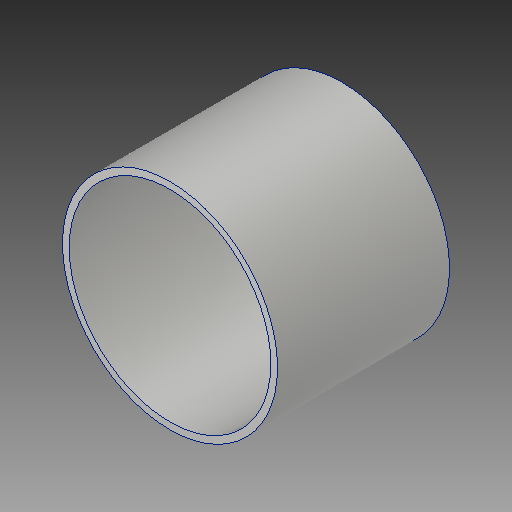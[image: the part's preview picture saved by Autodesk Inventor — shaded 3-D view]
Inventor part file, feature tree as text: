
AUTODESK INVENTOR PART (.ipt)
format: ipt  version: 2018 (Build 220112000, 112)  size: 125,952 bytes
history: native  units: in
note: dims shown in document units (in); Inventor stores cm internally (conversion verified against a paired STEP export)
features: extrude x1, sketch x1
ambient origin geometry x8: Origin, YZ Plane, XZ Plane, XY Plane, X Axis, Y Axis, Z Axis, Center Point
bodies: Solid1 (feature_tree)
feature tree (2):
  extrude  "Extrusion1"  Depth=3.2in
  sketch  "Sketch1"  dims[d0=4.0in d1=0.125in d2=3.2in d3=0.0in]
